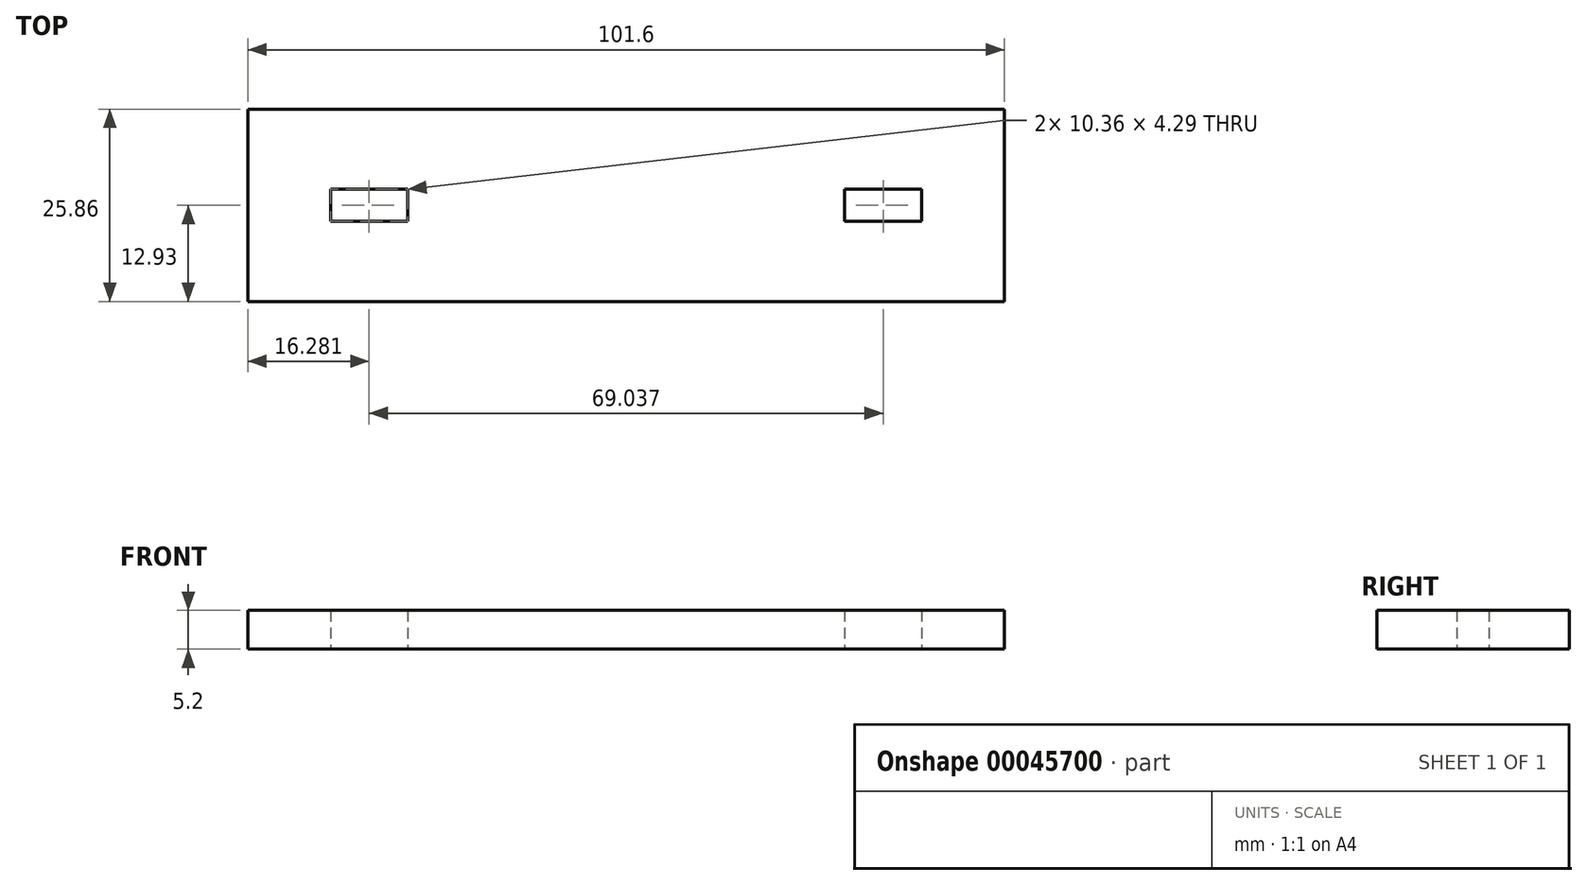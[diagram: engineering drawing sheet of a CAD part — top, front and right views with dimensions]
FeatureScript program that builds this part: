
annotation { "Feature Type Name" : "Feature", "Feature Type Description" : "" }
export const myFeature = defineFeature(function(context is Context, id is Id, definition is map)
    precondition{}
    {
        {
            var Q0;
            Q0=qCreatedBy(makeId("Top.planeOp"),FACE);
            var sketch = newSketch(context, id + "F0", { "sketchPlane" : qUnion([Q0])});
            skLineSegment(sketch, "E0.rect.bottom", {"start": v(-50.8, 12.93) * mm, "end": v(50.8, 12.93) * mm});
            skLineSegment(sketch, "E0.rect.top", {"start": v(-50.8, -12.93) * mm, "end": v(50.8, -12.93) * mm});
            skLineSegment(sketch, "E0.rect.left", {"start": v(-50.8, 12.93) * mm, "end": v(-50.8, -12.93) * mm});
            skLineSegment(sketch, "E0.rect.right", {"start": v(50.8, 12.93) * mm, "end": v(50.8, -12.93) * mm});
            skPoint(sketch, "E0.rect.middle", {"position": v(0, 0) * mm});
            skPoint(sketch, "E1.endSnap0", {"position": v(-50.8, 0) * mm});
            skLineSegment(sketch, "E2.top", {"start": v(39.7, 2.15) * mm, "end": v(29.34, 2.15) * mm});
            skLineSegment(sketch, "E2.left", {"start": v(39.7, 0) * mm, "end": v(39.7, 2.15) * mm});
            skLineSegment(sketch, "E2.right", {"start": v(29.34, 0) * mm, "end": v(29.34, 2.15) * mm});
            skLineSegment(sketch, "E3.top", {"start": v(39.7, -2.15) * mm, "end": v(29.34, -2.15) * mm});
            skLineSegment(sketch, "E3.left", {"start": v(39.7, 0) * mm, "end": v(39.7, -2.15) * mm});
            skLineSegment(sketch, "E3.right", {"start": v(29.34, 0) * mm, "end": v(29.34, -2.15) * mm});
            skLineSegment(sketch, "E4.MirrorCS", {"start": v(-39.7, 0) * mm, "end": v(-39.7, -2.15) * mm});
            skLineSegment(sketch, "E5.MirrorCS", {"start": v(-29.34, 0) * mm, "end": v(-29.34, 2.15) * mm});
            skLineSegment(sketch, "E6.MirrorCS", {"start": v(-39.7, 0) * mm, "end": v(-39.7, 2.15) * mm});
            skLineSegment(sketch, "E7.MirrorCS", {"start": v(-29.34, 0) * mm, "end": v(-29.34, -2.15) * mm});
            skLineSegment(sketch, "E8.MirrorCS", {"start": v(-39.7, -2.15) * mm, "end": v(-29.34, -2.15) * mm});
            skLineSegment(sketch, "E9.MirrorCS", {"start": v(-39.7, 2.15) * mm, "end": v(-29.34, 2.15) * mm});
            skSolve(sketch);
        }
        {
            var Q0;
            Q0=makeQuery(id+"F0.imprint","IMPRINT",FACE,{"disambiguationData":[TD([[makeQuery(id+"F0.imprint","IMPRINT",EDGE,{"derivedFrom":sQuery(id+"F0.wireOp",EDGE,"E0.rect.bottom")}),-1.0]])]});
            extrude(context, id + "F1", {"entities" : qUnion([Q0]), "depth" : 5.2 * mm});
        }
    });
